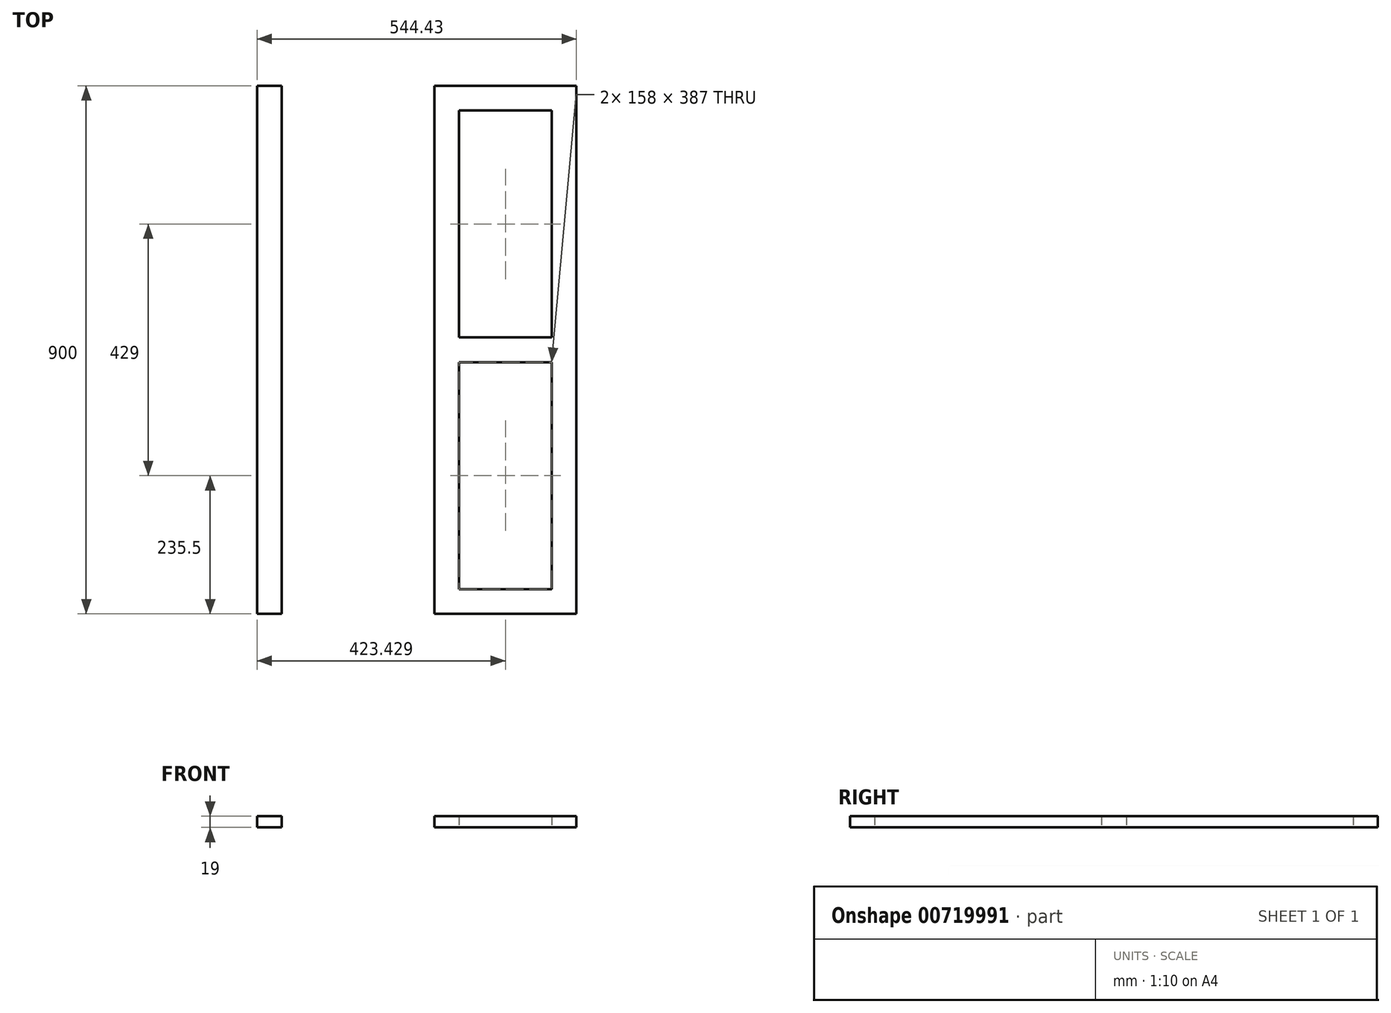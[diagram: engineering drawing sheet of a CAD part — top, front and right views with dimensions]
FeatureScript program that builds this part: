
annotation { "Feature Type Name" : "Feature", "Feature Type Description" : "" }
export const myFeature = defineFeature(function(context is Context, id is Id, definition is map)
    precondition{}
    {
        {
            var Q0;
            Q0=qCreatedBy(makeId("Top.planeOp"),FACE);
            var sketch = newSketch(context, id + "F0", { "sketchPlane" : qUnion([Q0])});
            skPoint(sketch, "E0.middle", {"position": v(93.88, 0) * mm});
            skPoint(sketch, "E1.left.start.orphan", {"position": v(24.31, 165.24) * mm});
            skPoint(sketch, "E0.right.start.orphan", {"position": v(-24.31, 165.24) * mm});
            skPoint(sketch, "E0.top.end.orphan", {"position": v(-24.31, -165.24) * mm});
            skPoint(sketch, "E2.left.start.orphan", {"position": v(24.31, -165.24) * mm});
            skLineSegment(sketch, "E3.bottom", {"start": v(172.88, 21) * mm, "end": v(14.88, 21) * mm});
            skLineSegment(sketch, "E3.top", {"start": v(172.88, -21) * mm, "end": v(14.88, -21) * mm});
            skLineSegment(sketch, "E3.left", {"start": v(172.88, 21) * mm, "end": v(172.88, -21) * mm});
            skLineSegment(sketch, "E3.right", {"start": v(14.88, 21) * mm, "end": v(14.88, -21) * mm});
            skLineSegment(sketch, "E4.bottom", {"start": v(172.88, 0) * mm, "end": v(214.88, 0) * mm});
            skLineSegment(sketch, "E4.top", {"start": v(172.88, 450) * mm, "end": v(214.88, 450) * mm});
            skLineSegment(sketch, "E4.left", {"start": v(172.88, 0) * mm, "end": v(172.88, 450) * mm});
            skLineSegment(sketch, "E4.right", {"start": v(214.88, 0) * mm, "end": v(214.88, 450) * mm});
            skLineSegment(sketch, "E5.top", {"start": v(172.88, -450) * mm, "end": v(214.88, -450) * mm});
            skLineSegment(sketch, "E5.left", {"start": v(172.88, 0) * mm, "end": v(172.88, -450) * mm});
            skLineSegment(sketch, "E5.right", {"start": v(214.88, 0) * mm, "end": v(214.88, -450) * mm});
            skLineSegment(sketch, "E6.bottom", {"start": v(172.88, 450) * mm, "end": v(14.88, 450) * mm});
            skLineSegment(sketch, "E6.top", {"start": v(172.88, 408) * mm, "end": v(14.88, 408) * mm});
            skLineSegment(sketch, "E6.left", {"start": v(172.88, 450) * mm, "end": v(172.88, 408) * mm});
            skLineSegment(sketch, "E6.right", {"start": v(14.88, 450) * mm, "end": v(14.88, 408) * mm});
            skLineSegment(sketch, "E7.bottom", {"start": v(172.88, -450) * mm, "end": v(14.88, -450) * mm});
            skLineSegment(sketch, "E7.top", {"start": v(172.88, -408) * mm, "end": v(14.88, -408) * mm});
            skLineSegment(sketch, "E7.left", {"start": v(172.88, -450) * mm, "end": v(172.88, -408) * mm});
            skLineSegment(sketch, "E7.right", {"start": v(14.88, -450) * mm, "end": v(14.88, -408) * mm});
            skLineSegment(sketch, "E8.bottom", {"start": v(14.88, -450) * mm, "end": v(-27.12, -450) * mm});
            skLineSegment(sketch, "E8.top", {"start": v(14.88, 0) * mm, "end": v(-27.12, 0) * mm});
            skLineSegment(sketch, "E8.left", {"start": v(14.88, -450) * mm, "end": v(14.88, 0) * mm});
            skLineSegment(sketch, "E8.right", {"start": v(-27.12, -450) * mm, "end": v(-27.12, 0) * mm});
            skLineSegment(sketch, "E9.bottom", {"start": v(14.88, 450) * mm, "end": v(-27.12, 450) * mm});
            skLineSegment(sketch, "E9.left", {"start": v(14.88, 450) * mm, "end": v(14.88, 0) * mm});
            skLineSegment(sketch, "E9.right", {"start": v(-27.12, 450) * mm, "end": v(-27.12, 0) * mm});
            skSolve(sketch);
        }
        {
            var Q0;
            Q0 = qSketchRegion(id + "F0", true);
            var Q1;
            {var subQ4=sQuery(id+"F0.wireOp",EDGE,"E3.bottom");Q1=makeQuery(id+"F0.imprint","IMPRINT",FACE,{"disambiguationData":[TD([[makeQuery(id+"F0.imprint","IMPRINT",EDGE,{"derivedFrom":subQ4}),1.0]])]});}
            extrude(context, id + "F1", {"entities" : qUnion([Q0, Q1]), "depth" : 19 * mm, "offsetDistance" : 25 * mm});
        }
        {
            var Q0;
            Q0=qCreatedBy(makeId("Top.planeOp"),FACE);
            var sketch = newSketch(context, id + "F2", { "sketchPlane" : qUnion([Q0])});
            skLineSegment(sketch, "E10.bottom", {"start": v(-287.55, 450) * mm, "end": v(-329.55, 450) * mm});
            skLineSegment(sketch, "E10.top", {"start": v(-287.55, -450) * mm, "end": v(-329.55, -450) * mm});
            skLineSegment(sketch, "E10.left", {"start": v(-287.55, 450) * mm, "end": v(-287.55, -450) * mm});
            skLineSegment(sketch, "E10.right", {"start": v(-329.55, 450) * mm, "end": v(-329.55, -450) * mm});
            skPoint(sketch, "E10.middle", {"position": v(-308.55, 0) * mm});
            skSolve(sketch);
        }
        {
            var Q0;
            Q0 = qSketchRegion(id + "F2", true);
            extrude(context, id + "F3", {"entities" : qUnion([Q0]), "depth" : 19 * mm, "offsetDistance" : 25 * mm});
        }
    });
